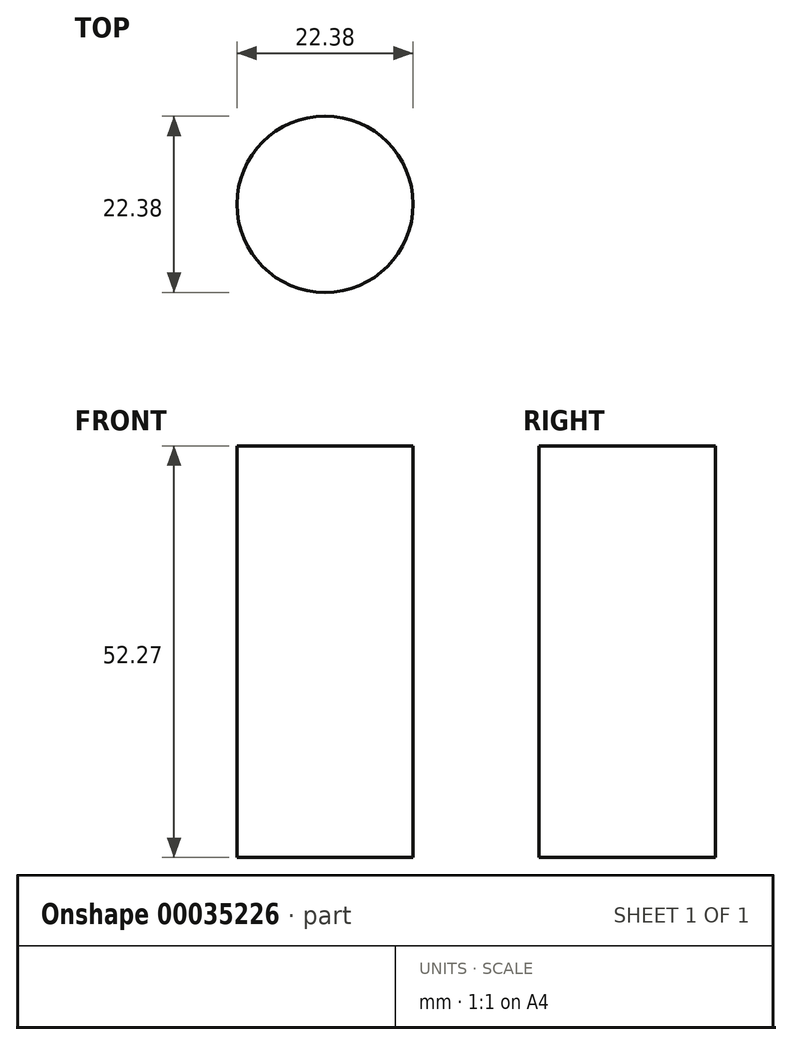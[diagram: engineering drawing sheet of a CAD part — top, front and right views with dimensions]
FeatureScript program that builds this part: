
annotation { "Feature Type Name" : "Feature", "Feature Type Description" : "" }
export const myFeature = defineFeature(function(context is Context, id is Id, definition is map)
    precondition{}
    {
        {
            var Q0;
            Q0=qCreatedBy(makeId("Front.planeOp"),FACE);
            var sketch = newSketch(context, id + "F0", { "sketchPlane" : qUnion([Q0])});
            skLineSegment(sketch, "E0", {"start": v(0, 0) * mm, "end": v(-11.2, 0) * mm});
            skLineSegment(sketch, "E1", {"start": v(-11.2, 0) * mm, "end": v(-11.2, 52.27) * mm});
            skLineSegment(sketch, "E2", {"start": v(0, 52.27) * mm, "end": v(-11.2, 52.27) * mm});
            skLineSegment(sketch, "E3", {"start": v(0, 52.27) * mm, "end": v(0, 0) * mm});
            skSolve(sketch);
        }
        {
            var Q0;
            Q0 = qSketchRegion(id + "F0", true);
            var Q1;
            Q1=sQuery(id+"F0.wireOp",EDGE,"E3");
            revolve(context, id + "F1", {"entities" : qUnion([Q0]), "axis" : qUnion([Q1]), "revolveType" : RevolveType.FULL});
        }
    });
